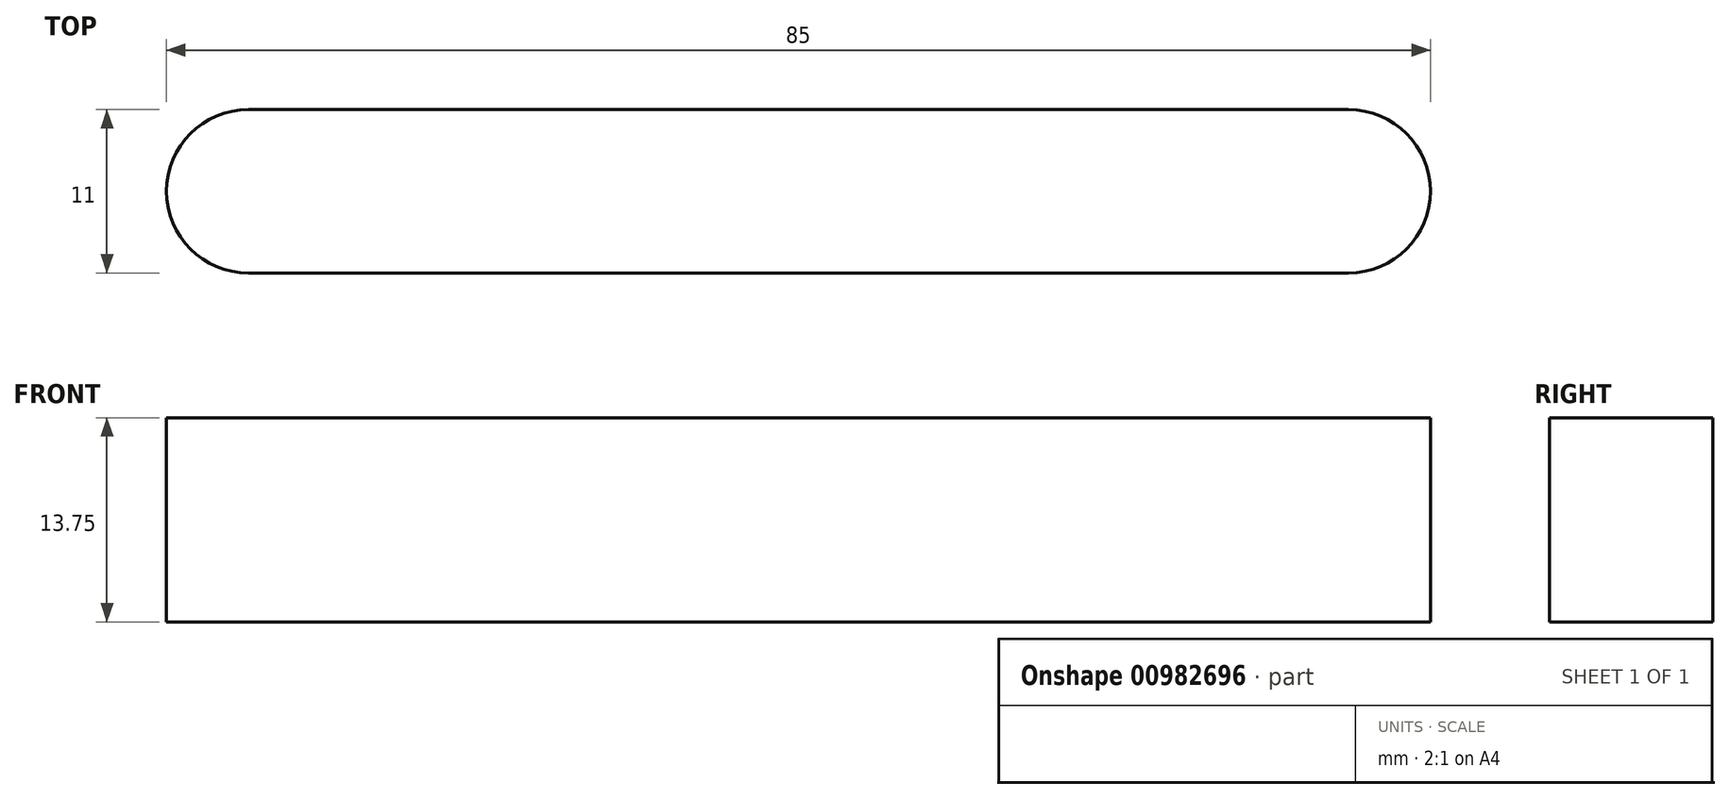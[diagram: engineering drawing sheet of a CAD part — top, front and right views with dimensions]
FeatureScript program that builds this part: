
annotation { "Feature Type Name" : "Feature", "Feature Type Description" : "" }
export const myFeature = defineFeature(function(context is Context, id is Id, definition is map)
    precondition{}
    {
        {
            var Q0;
            Q0=qCreatedBy(makeId("Top.planeOp"),FACE);
            var sketch = newSketch(context, id + "F0", { "sketchPlane" : qUnion([Q0])});
            skArc(sketch, "E0", {"start": v(0, 5.5) * mm, "mid": v(-5.5, 0) * mm, "end": v(0, -5.5) * mm});
            skArc(sketch, "E1", {"start": v(74, -5.5) * mm, "mid": v(79.5, 0) * mm, "end": v(74, 5.5) * mm});
            skLineSegment(sketch, "E2", {"start": v(0, -5.5) * mm, "end": v(74, -5.5) * mm});
            skLineSegment(sketch, "E3", {"start": v(74, 5.5) * mm, "end": v(0, 5.5) * mm});
            skSolve(sketch);
        }
        {
            var Q0;
            Q0=makeQuery(id+"F0.imprint","IMPRINT",FACE,{"disambiguationData":[TD([[makeQuery(id+"F0.imprint","IMPRINT",EDGE,{"derivedFrom":sQuery(id+"F0.wireOp",EDGE,"E0")}),1.0]])]});
            extrude(context, id + "F1", {"entities" : qUnion([Q0]), "depth" : 13.75 * mm, "offsetDistance" : 25 * mm});
        }
    });
